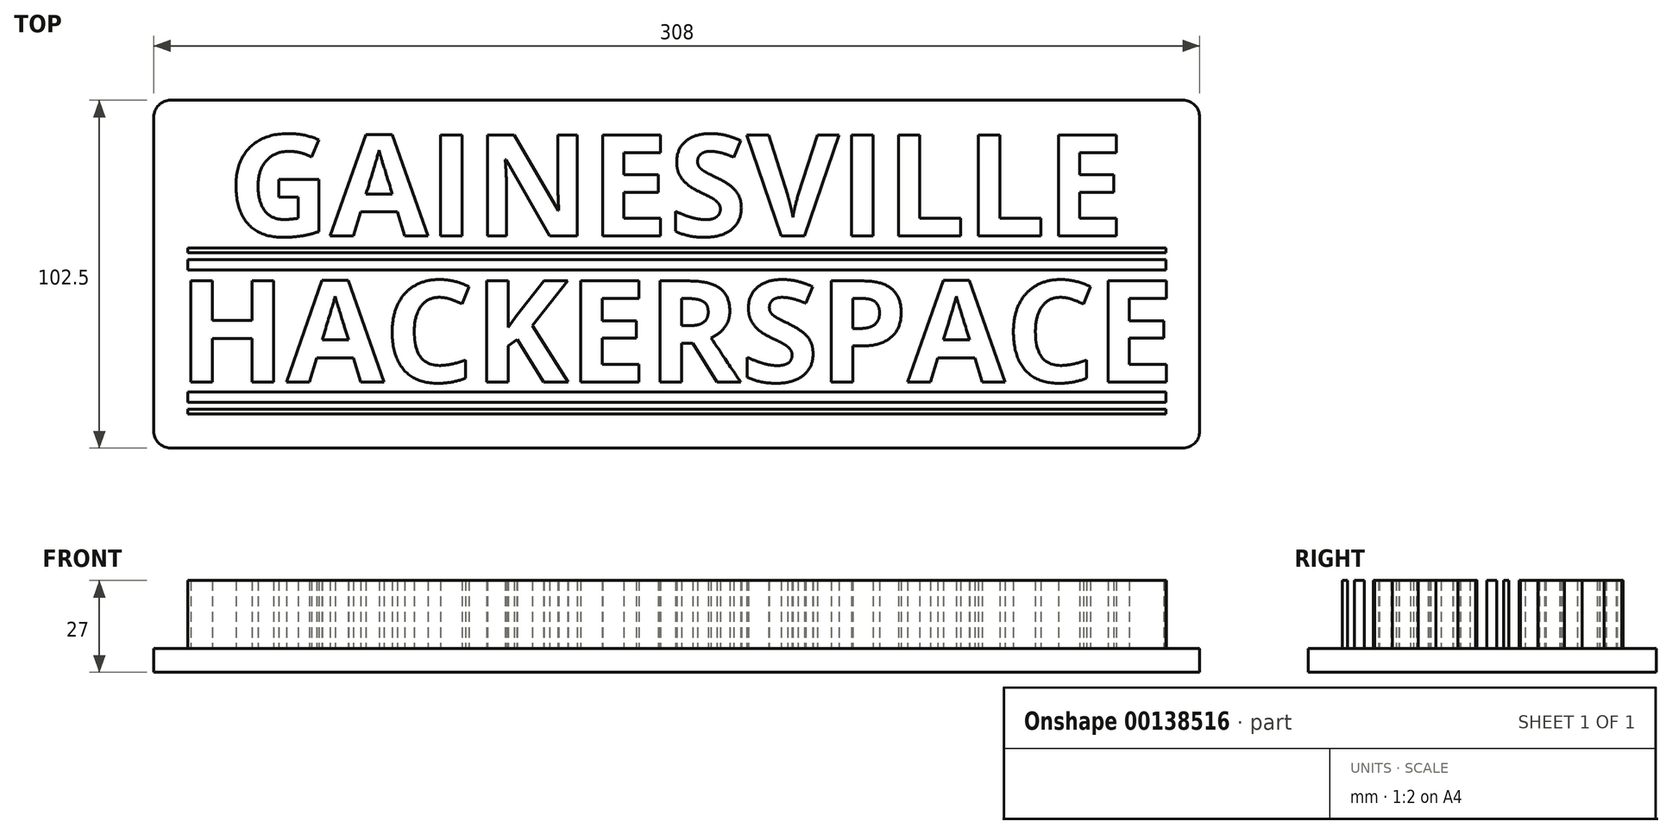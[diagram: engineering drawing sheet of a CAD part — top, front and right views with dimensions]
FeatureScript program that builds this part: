
annotation { "Feature Type Name" : "Feature", "Feature Type Description" : "" }
export const myFeature = defineFeature(function(context is Context, id is Id, definition is map)
    precondition{}
    {
        {
            var Q0;
            Q0=qCreatedBy(makeId("Top.planeOp"),FACE);
            var sketch = newSketch(context, id + "F0", { "sketchPlane" : qUnion([Q0])});
            skText(sketch, "E0", { "text": "GAINESVILLE", "fontName": "OpenSans-Bold.ttf"});
            skText(sketch, "E1", { "text": "HACKERSPACE", "fontName": "OpenSans-Bold.ttf"});
            skLineSegment(sketch, "E2", {"start": v(-146.84, -28) * mm, "end": v(146.84, -28) * mm, "construction": true});
            const initialGuessF0  = {"E0": [-0.1322, 0, 1, 0, 0.03], "E1": [-0.14684, -0.043, 1, 0, 0.03]};
            skSetInitialGuess(sketch, initialGuessF0);
            skSolve(sketch);
        }
        {
            var Q0;
            Q0=qCreatedBy(makeId("Top.planeOp"),FACE);
            var sketch = newSketch(context, id + "F1", { "sketchPlane" : qUnion([Q0])});
            skLineSegment(sketch, "E3.bottom", {"start": v(-144, -10) * mm, "end": v(144, -10) * mm});
            skLineSegment(sketch, "E3.top", {"start": v(-144, -7) * mm, "end": v(144, -7) * mm});
            skLineSegment(sketch, "E3.left", {"start": v(-144, -10) * mm, "end": v(-144, -7) * mm});
            skLineSegment(sketch, "E3.right", {"start": v(144, -10) * mm, "end": v(144, -7) * mm});
            skLineSegment(sketch, "E4.bottom", {"start": v(144, -5) * mm, "end": v(-144, -5) * mm});
            skLineSegment(sketch, "E4.top", {"start": v(144, -3.5) * mm, "end": v(-144, -3.5) * mm});
            skLineSegment(sketch, "E4.left", {"start": v(144, -5) * mm, "end": v(144, -3.5) * mm});
            skLineSegment(sketch, "E4.right", {"start": v(-144, -5) * mm, "end": v(-144, -3.5) * mm});
            skLineSegment(sketch, "E5", {"start": v(0, 0) * mm, "end": v(0, -12.93) * mm, "construction": true});
            skLineSegment(sketch, "E6", {"start": v(0, -7) * mm, "end": v(0, -10) * mm, "construction": true});
            skLineSegment(sketch, "E7", {"start": v(-150.46, -28) * mm, "end": v(156.53, -28) * mm, "construction": true});
            skLineSegment(sketch, "E8.MirrorCS", {"start": v(144, -46) * mm, "end": v(144, -49) * mm});
            skLineSegment(sketch, "E9.MirrorCS", {"start": v(-144, -46) * mm, "end": v(144, -46) * mm});
            skLineSegment(sketch, "E10.MirrorCS", {"start": v(-144, -49) * mm, "end": v(144, -49) * mm});
            skLineSegment(sketch, "E11.MirrorCS", {"start": v(-144, -46) * mm, "end": v(-144, -49) * mm});
            skLineSegment(sketch, "E12.MirrorCS", {"start": v(144, -52.5) * mm, "end": v(-144, -52.5) * mm});
            skLineSegment(sketch, "E13.MirrorCS", {"start": v(144, -51) * mm, "end": v(144, -52.5) * mm});
            skLineSegment(sketch, "E14.MirrorCS", {"start": v(144, -51) * mm, "end": v(-144, -51) * mm});
            skLineSegment(sketch, "E15.MirrorCS", {"start": v(-144, -51) * mm, "end": v(-144, -52.5) * mm});
            skSolve(sketch);
        }
        {
            var Q0;
            Q0=qCreatedBy(makeId("Top.planeOp"),FACE);
            var sketch = newSketch(context, id + "F2", { "sketchPlane" : qUnion([Q0])});
            skLineSegment(sketch, "E16.bottom", {"start": v(-149, 40) * mm, "end": v(149, 40) * mm});
            skLineSegment(sketch, "E16.top", {"start": v(-149, -62.5) * mm, "end": v(149, -62.5) * mm});
            skLineSegment(sketch, "E16.left", {"start": v(-154, 35) * mm, "end": v(-154, -57.5) * mm});
            skLineSegment(sketch, "E16.right", {"start": v(154, 35) * mm, "end": v(154, -57.5) * mm});
            skPoint(sketch, "E17.visualSharp", {"position": v(-154, 40) * mm});
            skArc(sketch, "E17.filletArc", {"start": v(-149, 40) * mm, "mid": v(-152.54, 38.54) * mm, "end": v(-154, 35) * mm});
            skPoint(sketch, "E18.visualSharp", {"position": v(154, 40) * mm});
            skArc(sketch, "E18.filletArc", {"start": v(154, 35) * mm, "mid": v(152.54, 38.54) * mm, "end": v(149, 40) * mm});
            skPoint(sketch, "E19.visualSharp", {"position": v(154, -62.5) * mm});
            skArc(sketch, "E19.filletArc", {"start": v(149, -62.5) * mm, "mid": v(152.54, -61.04) * mm, "end": v(154, -57.5) * mm});
            skPoint(sketch, "E20.visualSharp", {"position": v(-154, -62.5) * mm});
            skArc(sketch, "E20.filletArc", {"start": v(-154, -57.5) * mm, "mid": v(-152.54, -61.04) * mm, "end": v(-149, -62.5) * mm});
            skSolve(sketch);
        }
        {
            var Q0;
            Q0=makeQuery(id+"F2.imprint","IMPRINT",FACE,{"disambiguationData":[TD([[makeQuery(id+"F2.imprint","IMPRINT",EDGE,{"derivedFrom":sQuery(id+"F2.wireOp",EDGE,"E16.bottom")}),-1.0]])]});
            extrude(context, id + "F3", {"entities" : qUnion([Q0]), "depth" : 5 * mm});
        }
        {
            var Q0;
            Q0=makeQuery(id+"F3.opExtrude","CAP_FACE",FACE,{"disambiguationData":[OSD([sQuery(id+"F2.wireOp",EDGE,"E16.bottom"),sQuery(id+"F2.wireOp",EDGE,"E16.top"),sQuery(id+"F2.wireOp",EDGE,"E16.left"),sQuery(id+"F2.wireOp",EDGE,"E16.right"),sQuery(id+"F2.wireOp",EDGE,"E17.filletArc"),sQuery(id+"F2.wireOp",EDGE,"E18.filletArc"),sQuery(id+"F2.wireOp",EDGE,"E19.filletArc"),sQuery(id+"F2.wireOp",EDGE,"E20.filletArc")])],"isStart":true});
            extrude(context, id + "F4", {"entities" : qUnion([Q0]), "depth" : 2 * mm});
        }
        {
            var Q0;
            Q0 = qSketchRegion(id + "F0", true);
            extrude(context, id + "F5", {"entities" : qUnion([Q0]), "operationType" : NewBodyOperationType.ADD, "depth" : 25 * mm});
        }
        {
            var Q0;
            Q0 = qSketchRegion(id + "F1", true);
            extrude(context, id + "F6", {"entities" : qUnion([Q0]), "operationType" : NewBodyOperationType.ADD, "depth" : 25 * mm});
        }
    });
